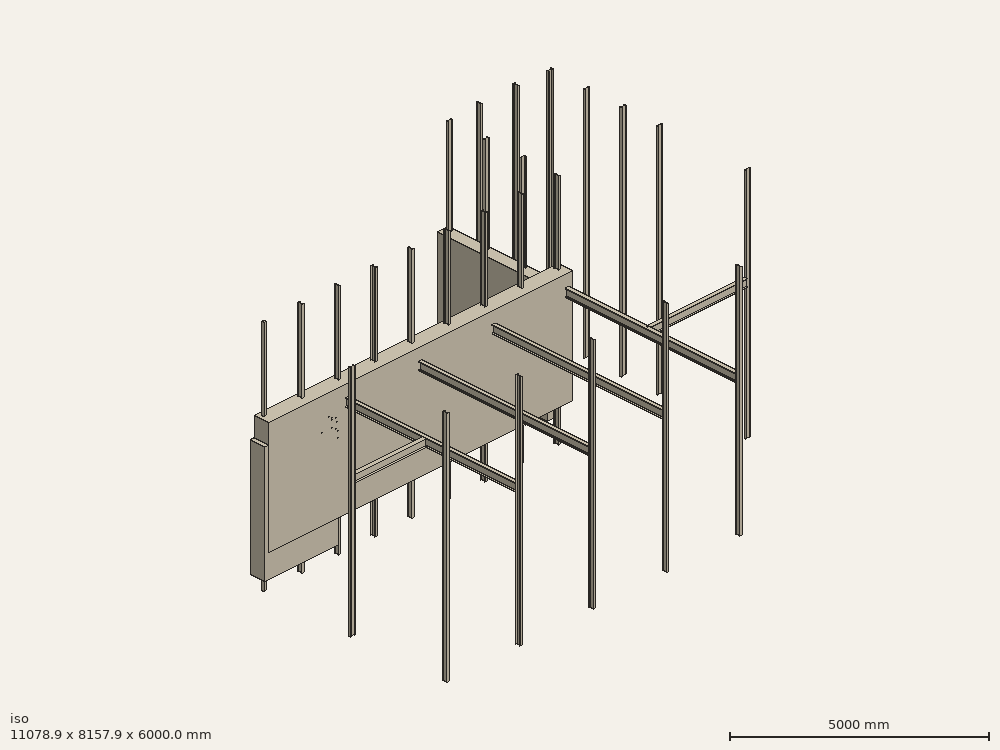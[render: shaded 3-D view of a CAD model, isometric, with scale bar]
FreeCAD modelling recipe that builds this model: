
FCSTD DOCUMENT  (FreeCAD 0.21R33321 (Git))
Label: 20230526-sunroom-layout
License: All rights reserved
LicenseURL: http://en.wikipedia.org/wiki/All_rights_reserved
objects: Part::Part2DObjectPython×75, Part::FeaturePython×34, App::DocumentObjectGroup×13, App::MeasureDistance×1, Spreadsheet::Sheet×1, App::GeometryPython×1
note: 110 computed .brp shape members not serialized (recipe doc carries the construction recipe); baked Part::Feature solids carry a one-line shape summary decoded from their .brp

FEATURE [Part::Part2DObjectPython] Rectangle001  label="Rect-sec1"  # Draft 2D object (typed FeaturePython)
  Area = 800000
  ChamferSize = 0
  Columns = 1
  FilletRadius = 0
  Height = 400
  Length = 2000
  MakeFace = true
  Placement = pos=(-5613.61,2200,0) rot=(0,0,1;0rad)
  Rows = 1
FEATURE [Part::FeaturePython] Structure001  label="fail"  # Arch/BIM 7 (typed FeaturePython)
  BaseMirror = false
  BaseOffsetX = 0
  BaseOffsetY = 0
  BasePerpendicularToTool = false
  BaseRotation = -21
  ComputedLength = 6000
  FaceMaker = 0
  Height = 64
  HorizontalArea = 4096
  IfcData = attributes={"GlobalId": {"name": "GlobalId", "type": "IfcGloballyUniqueId", "is_enum": false, "enum_values": []}, "Description": {"... (+475 chars omitted),+1 more (map truncated)
  IfcType = 7
  Length = 6000
  MoveBase = false
  MoveWithHost = false
  Nodes = (2) [(-3.54371e-32,-1.11022e-15,8.32667e-16),(6000,-1.11022e-15,8.32667e-16)]
  NodesOffset = 0
  Normal = (0,0,0)
  PerimeterLength = 256
  Placement = pos=(-5368,2460,5000) rot=(0,1,0;1.5708rad)
  PredefinedType = 0
  Profile = IPE120
  ToolOffsetFirst = 0
  ToolOffsetLast = 0
  VerticalArea = 1536000
  Width = 64
  expr: Profile = Spreadsheet.vertcoltype
FEATURE [Part::FeaturePython] Wall  label="NorthWall1-400mm"  # Arch/BIM 166 (typed FeaturePython)
  Align = 2
  Area = 0
  Base = -> Rectangle001
  BlockHeight = 0
  BlockLength = 0
  CountBroken = 0
  CountEntire = 0
  Face = 0
  Height = 3000
  HorizontalArea = 800000
  IfcData = attributes={"GlobalId": {"name": "GlobalId", "type": "IfcGloballyUniqueId", "is_enum": false, "enum_values": []}, "Description": {"... (+533 chars omitted),+1 more (map truncated)
  IfcType = 166
  Joint = 0
  Length = 0
  MakeBlocks = false
  MoveBase = false
  MoveWithHost = false
  Normal = (0,0,0)
  OffsetFirst = 0
  OffsetSecond = 0
  PerimeterLength = 4800
  Placement = pos=(0,0,-600) rot=(0,0,1;0rad)
  PredefinedType = 0
  VerticalArea = 1.44e+07
  Width = 200
FEATURE [App::MeasureDistance] Distance  label="Distance: 2363.01 mm"
  Distance = 2398.43
  P1 = (-3738.2,2140,2600)
  P2 = (-3709.77,2140,4998.26)
FEATURE [Spreadsheet::Sheet] Spreadsheet  label="S"
  cells = A1=BaseHeight; B1(BaseHeight)==5200 mm; A2=BaseLength; B2(BaseLength)==11000 mm; A3=BaseSlabThickness; B3(BaseSlabThickness)==200 mm; A4=ColHeight; B4(ColHeight)==6000 mm; A5=NorthWallThickness; B5(NorthWallThickness)==400 mm; A6=SouthWallThickness; B6(SouthWallThickness)==200 mm; A7=LaundryRoomWidth; B7(LaundryRoomWidth)==3 m; A8=LaundryRoomDepth; B8(LaundryRoomDepth)==3 m; A9=col1xpos; B9(col1xpos)==-BaseLength / 2 + 100 mm; A10=col1ypos; B10(col1ypos)==BaseHeight / 2 - NorthWallThickness / 2; A11=col1xposIPE; B11(col1xposIPE)==col1xpos + 32 mm; A12=col1yposIPE; B12(col1yposIPE)==col1ypos + 60 mm; A13=colwidth; B13(colwidth)==64 mm; A14=colheight; B14(collength)==120 mm; A15=vertcoltype; B15(vertcoltype)=IPE120
FEATURE [Part::Part2DObjectPython] Rectangle003  label="NorthWallRect"  # Draft 2D object (typed FeaturePython)
  Area = 3320000
  ChamferSize = 0
  Columns = 1
  FilletRadius = 0
  Height = 400
  Length = 8300
  MakeFace = true
  Placement = pos=(-5500,2200,0) rot=(0,0,1;0rad)
  Rows = 1
  expr: .Placement.Base.x = -Spreadsheet.BaseLength / 2
  expr: .Placement.Base.y = Spreadsheet.BaseHeight / 2 - Spreadsheet.NorthWallThickness
  expr: Height = Spreadsheet.NorthWallThickness
  expr: Length = Spreadsheet.BaseLength - 3 m + 300 mm
FEATURE [Part::Part2DObjectPython] Rectangle004  label="SouthWallRect"  # Draft 2D object (typed FeaturePython)
  Area = 2200000
  ChamferSize = 0
  Columns = 1
  FilletRadius = 0
  Height = 200
  Length = 11000
  MakeFace = true
  Placement = pos=(-5500,-2600,0) rot=(0,0,1;0rad)
  Rows = 1
  expr: .Placement.Base.x = -Spreadsheet.BaseLength / 2
  expr: .Placement.Base.y = -Spreadsheet.BaseHeight / 2
  expr: Height = Spreadsheet.SouthWallThickness
  expr: Length = Spreadsheet.BaseLength
FEATURE [Part::Part2DObjectPython] Rectangle005  label="NorthColPosRect"  # Draft 2D object (typed FeaturePython)
  Area = 960000
  ChamferSize = 0
  Columns = 1
  FilletRadius = 0
  Height = 120
  Length = 8000
  MakeFace = true
  Placement = pos=(-5500,2400,0) rot=(0,0,1;0rad)
  Rows = 1
  expr: .Placement.Base.x = -Spreadsheet.BaseLength / 2
  expr: .Placement.Base.y = Spreadsheet.BaseHeight / 2 - Spreadsheet.NorthWallThickness / 2
FEATURE [Part::Part2DObjectPython] Rectangle006  label="WestWallRect"  # Draft 2D object (typed FeaturePython)
  Area = 920000
  ChamferSize = 0
  Columns = 1
  FilletRadius = 0
  Height = 4600
  Length = 200
  MakeFace = true
  Placement = pos=(-5500,-2400,0) rot=(0,0,1;0rad)
  Rows = 1
  expr: Height = Spreadsheet.BaseHeight - Spreadsheet.NorthWallThickness - Spreadsheet.SouthWallThickness
  expr: Length = Spreadsheet.SouthWallThickness
FEATURE [Part::Part2DObjectPython] Rectangle007  label="Col1Rect"  # Draft 2D object (typed FeaturePython)
  Area = 7680
  ChamferSize = 0
  Columns = 1
  FilletRadius = 0
  Height = 120
  Length = 64
  MakeFace = true
  Placement = pos=(-5400,2400,0) rot=(0,0,1;0rad)
  Rows = 1
  expr: .Placement.Base.x = Spreadsheet.col1xpos
  expr: .Placement.Base.y = Spreadsheet.col1ypos
  expr: Height = Spreadsheet.collength
  expr: Length = Spreadsheet.colwidth
FEATURE [Part::Part2DObjectPython] Clone2D  label="Col2Rect (2D)"  # Draft 2D object (typed FeaturePython)
  Fuse = false
  Objects = -> [Rectangle007]
  Placement = pos=(-4400,2400,0) rot=(0,0,1;0rad)
  Scale = (1,1,1)
  expr: .Placement.Base.x = Spreadsheet.col1xpos + 1000 mm
  expr: .Placement.Base.y = Spreadsheet.col1ypos
FEATURE [Part::Part2DObjectPython] Clone2D001  label="Col3Rect (2D)"  # Draft 2D object (typed FeaturePython)
  Fuse = false
  Objects = -> [Rectangle007]
  Placement = pos=(-3400,2400,0) rot=(0,0,1;0rad)
  Scale = (1,1,1)
  expr: .Placement.Base.x = Spreadsheet.col1xpos + 2000 mm
FEATURE [Part::Part2DObjectPython] Clone2D002  label="Col4Rect (2D)"  # Draft 2D object (typed FeaturePython)
  Fuse = false
  Objects = -> [Rectangle007]
  Placement = pos=(-2400,2400,0) rot=(0,0,1;0rad)
  Scale = (1,1,1)
  expr: .Placement.Base.x = Spreadsheet.col1xpos + 3000 mm
  expr: .Placement.Base.y = Spreadsheet.col1ypos
FEATURE [Part::Part2DObjectPython] Clone2D003  label="Col5Rect (2D)"  # Draft 2D object (typed FeaturePython)
  Fuse = false
  Objects = -> [Rectangle007]
  Placement = pos=(-1400,2400,0) rot=(0,0,1;0rad)
  Scale = (1,1,1)
  expr: .Placement.Base.x = Spreadsheet.col1xpos + 4000 mm
  expr: .Placement.Base.y = Spreadsheet.col1ypos
FEATURE [Part::Part2DObjectPython] Clone2D004  label="Col7Rect (2D)"  # Draft 2D object (typed FeaturePython)
  Fuse = false
  Objects = -> [Rectangle007]
  Placement = pos=(600,2400,0) rot=(0,0,1;0rad)
  Scale = (1,1,1)
  expr: .Placement.Base.x = Spreadsheet.col1xpos + 6000 mm
  expr: .Placement.Base.y = Spreadsheet.col1ypos
FEATURE [Part::Part2DObjectPython] Clone2D005  label="Col6Rect (2D)"  # Draft 2D object (typed FeaturePython)
  Fuse = false
  Objects = -> [Rectangle007]
  Placement = pos=(-400,2400,0) rot=(0,0,1;0rad)
  Scale = (1,1,1)
  expr: .Placement.Base.x = Spreadsheet.col1xpos + 5000 mm
  expr: .Placement.Base.y = Spreadsheet.col1ypos
FEATURE [Part::Part2DObjectPython] Clone2D006  label="Col8Rect (2D)"  # Draft 2D object (typed FeaturePython)
  Fuse = false
  Objects = -> [Rectangle007]
  Placement = pos=(1600,2400,0) rot=(0,0,1;0rad)
  Scale = (1,1,1)
  expr: .Placement.Base.x = Spreadsheet.col1xpos + 7000 mm
  expr: .Placement.Base.y = Spreadsheet.col1ypos
FEATURE [Part::Part2DObjectPython] Rectangle008  label="LaundryRoomRect"  # Draft 2D object (typed FeaturePython)
  Area = 9000000
  ChamferSize = 0
  Columns = 1
  FilletRadius = 0
  Height = 3000
  Length = 3000
  MakeFace = true
  Placement = pos=(2500,2600,0) rot=(0,0,1;0rad)
  Rows = 1
  expr: .Placement.Base.x = 2500
  expr: Height = Spreadsheet.LaundryRoomDepth
  expr: Length = Spreadsheet.LaundryRoomDepth
FEATURE [Part::Part2DObjectPython] Clone2D007  label="Col9Rect (2D)"  # Draft 2D object (typed FeaturePython)
  Fuse = false
  Objects = -> [Rectangle007]
  Placement = pos=(2602.84,2400.21,0) rot=(0,0,1;0rad)
  Scale = (1,1,1)
FEATURE [App::DocumentObjectGroup] Group001  label="RectN"
  Group = -> [Rectangle007,Clone2D,Clone2D001,Clone2D002,Clone2D003,Clone2D005,Clone2D004,Clone2D006,Clone2D007]
FEATURE [Part::Part2DObjectPython] Clone2D008  label="Col10Rect (2D)"  # Draft 2D object (typed FeaturePython)
  Fuse = false
  Objects = -> [Clone2D007]
  Placement = pos=(2720,3400,0) rot=(0,0,1;1.5708rad)
  Scale = (1,1,1)
  expr: .Placement.Base.x = 2720 mm
  expr: .Placement.Base.y = 2400 mm + 1000 mm
FEATURE [Part::Part2DObjectPython] IPE120005  # Draft 2D object (typed FeaturePython)
  FlangeThickness = 6.3
  Height = 120
  WebThickness = 4.4
  Width = 64
FEATURE [Part::FeaturePython] Structure006  label="Col5"  # Arch/BIM 24 (typed FeaturePython)
  Base = -> IPE120005
  BaseMirror = false
  BaseOffsetX = 0
  BaseOffsetY = 0
  BasePerpendicularToTool = false
  BaseRotation = 0
  ComputedLength = 6000
  FaceMaker = 0
  Height = 6000
  HorizontalArea = 1278.96
  IfcData = attributes={"GlobalId": {"name": "GlobalId", "type": "IfcGloballyUniqueId", "is_enum": false, "enum_values": []}, "Description": {"... (+438 chars omitted),+1 more (map truncated)
  IfcType = 24
  Length = 120
  MoveBase = false
  MoveWithHost = false
  Nodes = (2) [(0,-1.61713e-15,0),(0,-1.61713e-15,6000)]
  NodesOffset = 0
  Normal = (0,0,0)
  PerimeterLength = 487.2
  Placement = pos=(-1368,2460,-1000) rot=(0,0,1;0rad)
  PredefinedType = 0
  Profile = IPE120
  ToolOffsetFirst = 0
  ToolOffsetLast = 0
  VerticalArea = 2923200
  Width = 64
  expr: .Placement.Base.x = Spreadsheet.col1xposIPE + 4000 mm
  expr: .Placement.Base.y = Spreadsheet.col1yposIPE
FEATURE [Part::Part2DObjectPython] IPE120006  # Draft 2D object (typed FeaturePython)
  FlangeThickness = 6.3
  Height = 120
  WebThickness = 4.4
  Width = 64
FEATURE [Part::FeaturePython] Structure007  label="Col6"  # Arch/BIM 24 (typed FeaturePython)
  Base = -> IPE120006
  BaseMirror = false
  BaseOffsetX = 0
  BaseOffsetY = 0
  BasePerpendicularToTool = false
  BaseRotation = 0
  ComputedLength = 6000
  FaceMaker = 0
  Height = 6000
  HorizontalArea = 1278.96
  IfcData = attributes={"GlobalId": {"name": "GlobalId", "type": "IfcGloballyUniqueId", "is_enum": false, "enum_values": []}, "Description": {"... (+438 chars omitted),+1 more (map truncated)
  IfcType = 24
  Length = 120
  MoveBase = false
  MoveWithHost = false
  Nodes = (2) [(0,-1.61713e-15,0),(0,-1.61713e-15,6000)]
  NodesOffset = 0
  Normal = (0,0,0)
  PerimeterLength = 487.2
  Placement = pos=(-368,2460,-1000) rot=(0,0,1;0rad)
  PredefinedType = 0
  Profile = IPE120
  ToolOffsetFirst = 0
  ToolOffsetLast = 0
  VerticalArea = 2923200
  Width = 64
  expr: .Placement.Base.x = Spreadsheet.col1xposIPE + 5000 mm
  expr: .Placement.Base.y = Spreadsheet.col1yposIPE
FEATURE [Part::Part2DObjectPython] IPE120007  # Draft 2D object (typed FeaturePython)
  FlangeThickness = 6.3
  Height = 120
  WebThickness = 4.4
  Width = 64
FEATURE [Part::FeaturePython] Structure008  label="Col7"  # Arch/BIM 24 (typed FeaturePython)
  Base = -> IPE120007
  BaseMirror = false
  BaseOffsetX = 0
  BaseOffsetY = 0
  BasePerpendicularToTool = false
  BaseRotation = 0
  ComputedLength = 6000
  FaceMaker = 0
  Height = 6000
  HorizontalArea = 1278.96
  IfcData = attributes={"GlobalId": {"name": "GlobalId", "type": "IfcGloballyUniqueId", "is_enum": false, "enum_values": []}, "Description": {"... (+438 chars omitted),+1 more (map truncated)
  IfcType = 24
  Length = 120
  MoveBase = false
  MoveWithHost = false
  Nodes = (2) [(0,-1.61713e-15,0),(0,-1.61713e-15,6000)]
  NodesOffset = 0
  Normal = (0,0,0)
  PerimeterLength = 487.2
  Placement = pos=(632,2460,-1000) rot=(0,0,1;0rad)
  PredefinedType = 0
  Profile = IPE120
  ToolOffsetFirst = 0
  ToolOffsetLast = 0
  VerticalArea = 2923200
  Width = 64
  expr: .Placement.Base.x = Spreadsheet.col1xposIPE + 6000 mm
  expr: .Placement.Base.y = Spreadsheet.col1yposIPE
FEATURE [Part::Part2DObjectPython] IPE120008  # Draft 2D object (typed FeaturePython)
  FlangeThickness = 6.3
  Height = 120
  WebThickness = 4.4
  Width = 64
FEATURE [Part::FeaturePython] Structure009  label="Col8"  # Arch/BIM 24 (typed FeaturePython)
  Base = -> IPE120008
  BaseMirror = false
  BaseOffsetX = 0
  BaseOffsetY = 0
  BasePerpendicularToTool = false
  BaseRotation = 0
  ComputedLength = 6000
  FaceMaker = 0
  Height = 6000
  HorizontalArea = 1278.96
  IfcData = attributes={"GlobalId": {"name": "GlobalId", "type": "IfcGloballyUniqueId", "is_enum": false, "enum_values": []}, "Description": {"... (+438 chars omitted),+1 more (map truncated)
  IfcType = 24
  Length = 120
  MoveBase = false
  MoveWithHost = false
  Nodes = (2) [(0,-1.61713e-15,0),(0,-1.61713e-15,6000)]
  NodesOffset = 0
  Normal = (0,0,0)
  PerimeterLength = 487.2
  Placement = pos=(1632,2460,-1000) rot=(0,0,1;0rad)
  PredefinedType = 0
  Profile = IPE120
  ToolOffsetFirst = 0
  ToolOffsetLast = 0
  VerticalArea = 2923200
  Width = 64
  expr: .Placement.Base.x = Spreadsheet.col1xposIPE + 7000 mm
  expr: .Placement.Base.y = Spreadsheet.col1yposIPE
FEATURE [Part::Part2DObjectPython] IPE120009  # Draft 2D object (typed FeaturePython)
  FlangeThickness = 6.3
  Height = 120
  WebThickness = 4.4
  Width = 64
FEATURE [Part::FeaturePython] Structure010  label="Col9"  # Arch/BIM 24 (typed FeaturePython)
  Base = -> IPE120009
  BaseMirror = false
  BaseOffsetX = 0
  BaseOffsetY = 0
  BasePerpendicularToTool = false
  BaseRotation = 0
  ComputedLength = 6000
  FaceMaker = 0
  Height = 6000
  HorizontalArea = 1278.96
  IfcData = attributes={"GlobalId": {"name": "GlobalId", "type": "IfcGloballyUniqueId", "is_enum": false, "enum_values": []}, "Description": {"... (+438 chars omitted),+1 more (map truncated)
  IfcType = 24
  Length = 120
  MoveBase = false
  MoveWithHost = false
  Nodes = (2) [(0,-1.61713e-15,0),(0,-1.61713e-15,6000)]
  NodesOffset = 0
  Normal = (0,0,0)
  PerimeterLength = 487.2
  Placement = pos=(2634.76,2460.15,-1000) rot=(0,0,1;0rad)
  PredefinedType = 0
  Profile = IPE120
  ToolOffsetFirst = 0
  ToolOffsetLast = 0
  VerticalArea = 2923200
  Width = 64
FEATURE [Part::Part2DObjectPython] Rectangle009  label="LaundryWallWestRect"  # Draft 2D object (typed FeaturePython)
  Area = 900000
  ChamferSize = 0
  Columns = 1
  FilletRadius = 0
  Height = 3000
  Length = 300
  MakeFace = true
  Placement = pos=(2500.39,2600,0) rot=(0,0,1;0rad)
  Rows = 1
  expr: Height = Spreadsheet.LaundryRoomDepth
FEATURE [Part::Part2DObjectPython] Clone2D009  label="Col11Rect (2D)"  # Draft 2D object (typed FeaturePython)
  Fuse = false
  Objects = -> [Clone2D008]
  Placement = pos=(2720,4400,0) rot=(0,0,1;1.5708rad)
  Scale = (1,1,1)
  expr: .Placement.Base.y = 2400 mm + 2000 mm
FEATURE [Part::Part2DObjectPython] Clone2D010  label="Col12Rect (2D)"  # Draft 2D object (typed FeaturePython)
  Fuse = false
  Objects = -> [Clone2D009]
  Placement = pos=(2720,5400,0) rot=(0,0,1;1.5708rad)
  Scale = (1,1,1)
  expr: .Placement.Base.y = 2400 mm + 3000 mm
FEATURE [Part::Part2DObjectPython] Rectangle010  label="LaundryWallEastRect"  # Draft 2D object (typed FeaturePython)
  Area = 600000
  ChamferSize = 0
  Columns = 1
  FilletRadius = 0
  Height = 3000
  Length = 200
  MakeFace = true
  Placement = pos=(5300,2600,0) rot=(0,0,1;0rad)
  Rows = 1
  expr: Height = Spreadsheet.LaundryRoomDepth
FEATURE [Part::Part2DObjectPython] Clone2D011  label="Col15Rect (2D)"  # Draft 2D object (typed FeaturePython)
  Fuse = false
  Objects = -> [Clone2D010]
  Placement = pos=(5465.32,5400,0) rot=(0,0,1;1.5708rad)
  Scale = (1,1,1)
FEATURE [Part::Part2DObjectPython] Clone2D012  label="Col16Rect (2D)"  # Draft 2D object (typed FeaturePython)
  Fuse = false
  Objects = -> [Clone2D009]
  Placement = pos=(5465.32,4400,0) rot=(0,0,1;1.5708rad)
  Scale = (1,1,1)
FEATURE [Part::Part2DObjectPython] Clone2D013  label="Col17Rect (2D)"  # Draft 2D object (typed FeaturePython)
  Fuse = false
  Objects = -> [Clone2D008]
  Placement = pos=(5465.32,3400,0) rot=(0,0,1;1.5708rad)
  Scale = (1,1,1)
FEATURE [Part::Part2DObjectPython] Clone2D014  label="Col14Rect (2D)"  # Draft 2D object (typed FeaturePython)
  Fuse = false
  Objects = -> [Clone2D006]
  Placement = pos=(4509.76,5428.53,0) rot=(0,0,1;0rad)
  Scale = (1,1,1)
FEATURE [Part::Part2DObjectPython] Clone2D015  label="Col13Rect (2D)"  # Draft 2D object (typed FeaturePython)
  Fuse = false
  Objects = -> [Clone2D004]
  Placement = pos=(3509.76,5428.53,0) rot=(0,0,1;0rad)
  Scale = (1,1,1)
FEATURE [App::DocumentObjectGroup] Group004  label="Rect"
  Group = -> [Clone2D010,Clone2D009,Clone2D008,Clone2D011,Clone2D012,Clone2D013,Clone2D014,Clone2D015]
FEATURE [Part::Part2DObjectPython] Rectangle011  label="EastWallRect"  # Draft 2D object (typed FeaturePython)
  Area = 1000000
  ChamferSize = 0
  Columns = 1
  FilletRadius = 0
  Height = 5000
  Length = 200
  MakeFace = true
  Placement = pos=(5300,-2400,0) rot=(0,0,1;0rad)
  Rows = 1
FEATURE [App::GeometryPython] BuildingPart  label="Floor"  # Arch/BIM 14 (typed FeaturePython)
  Area = 0
  CompositionType = 0
  Elevation = 0
  Group = -> [Rectangle005,Rectangle011,Rectangle004,Rectangle008,Rectangle009,Rectangle010,Rectangle006]
  Height = 0
  HeightPropagate = true
  IfcData = attributes={"GlobalId": {"name": "GlobalId", "type": "IfcGloballyUniqueId", "is_enum": false, "enum_values": []}, "Description": {"... (+866 chars omitted),+1 more (map truncated)
  IfcType = 14
  LevelOffset = 0
  LongName = Floor
  OnlySolids = true
  expr: Elevation = .Placement.Base.z
FEATURE [Part::Part2DObjectPython] Clone2D016  label="Col18Rect (2D)"  # Draft 2D object (typed FeaturePython)
  Fuse = false
  Objects = -> [Clone2D007]
  Placement = pos=(5460,2400,0) rot=(0,0,1;1.5708rad)
  Scale = (1,1,1)
FEATURE [Part::Part2DObjectPython] IPE120011  # Draft 2D object (typed FeaturePython)
  FlangeThickness = 6.3
  Height = 120
  WebThickness = 4.4
  Width = 64
FEATURE [Part::FeaturePython] Structure011  label="Col13"  # Arch/BIM 24 (typed FeaturePython)
  Base = -> IPE120011
  BaseMirror = false
  BaseOffsetX = 0
  BaseOffsetY = 0
  BasePerpendicularToTool = false
  BaseRotation = 0
  ComputedLength = 6000
  FaceMaker = 0
  Height = 6000
  HorizontalArea = 1278.96
  IfcData = attributes={"GlobalId": {"name": "GlobalId", "type": "IfcGloballyUniqueId", "is_enum": false, "enum_values": []}, "Description": {"... (+438 chars omitted),+1 more (map truncated)
  IfcType = 24
  Length = 120
  MoveBase = false
  MoveWithHost = false
  Nodes = (2) [(0,-1.61713e-15,0),(0,-1.61713e-15,6000)]
  NodesOffset = 0
  Normal = (0,0,0)
  PerimeterLength = 487.2
  Placement = pos=(3541.76,5488.53,-1000) rot=(0,0,-1;0rad)
  PredefinedType = 0
  Profile = IPE120
  ToolOffsetFirst = 0
  ToolOffsetLast = 0
  VerticalArea = 2923200
  Width = 64
FEATURE [Part::Part2DObjectPython] IPE120012  # Draft 2D object (typed FeaturePython)
  FlangeThickness = 6.3
  Height = 120
  WebThickness = 4.4
  Width = 64
FEATURE [Part::FeaturePython] Structure012  label="Col14"  # Arch/BIM 24 (typed FeaturePython)
  Base = -> IPE120012
  BaseMirror = false
  BaseOffsetX = 0
  BaseOffsetY = 0
  BasePerpendicularToTool = false
  BaseRotation = 0
  ComputedLength = 6000
  FaceMaker = 0
  Height = 6000
  HorizontalArea = 1278.96
  IfcData = attributes={"GlobalId": {"name": "GlobalId", "type": "IfcGloballyUniqueId", "is_enum": false, "enum_values": []}, "Description": {"... (+438 chars omitted),+1 more (map truncated)
  IfcType = 24
  Length = 120
  MoveBase = false
  MoveWithHost = false
  Nodes = (2) [(0,-1.61713e-15,0),(0,-1.61713e-15,6000)]
  NodesOffset = 0
  Normal = (0,0,0)
  PerimeterLength = 487.2
  Placement = pos=(4541.76,5488.53,-1000) rot=(0,0,1;0rad)
  PredefinedType = 0
  Profile = IPE120
  ToolOffsetFirst = 0
  ToolOffsetLast = 0
  VerticalArea = 2923200
  Width = 64
FEATURE [Part::Part2DObjectPython] IPE120013  # Draft 2D object (typed FeaturePython)
  FlangeThickness = 6.3
  Height = 120
  WebThickness = 4.4
  Width = 64
FEATURE [Part::FeaturePython] Structure013  label="Col12"  # Arch/BIM 24 (typed FeaturePython)
  Base = -> IPE120013
  BaseMirror = false
  BaseOffsetX = 0
  BaseOffsetY = 0
  BasePerpendicularToTool = false
  BaseRotation = 0
  ComputedLength = 6000
  FaceMaker = 0
  Height = 6000
  HorizontalArea = 1278.96
  IfcData = attributes={"GlobalId": {"name": "GlobalId", "type": "IfcGloballyUniqueId", "is_enum": false, "enum_values": []}, "Description": {"... (+438 chars omitted),+1 more (map truncated)
  IfcType = 24
  Length = 120
  MoveBase = false
  MoveWithHost = false
  Nodes = (2) [(0,-1.61713e-15,0),(0,-1.61713e-15,6000)]
  NodesOffset = 0
  Normal = (0,0,0)
  PerimeterLength = 487.2
  Placement = pos=(2660,5432,-1000) rot=(0,0,1;1.5708rad)
  PredefinedType = 0
  Profile = IPE120
  ToolOffsetFirst = 0
  ToolOffsetLast = 0
  VerticalArea = 2923200
  Width = 64
FEATURE [Part::Part2DObjectPython] IPE120014  # Draft 2D object (typed FeaturePython)
  FlangeThickness = 6.3
  Height = 120
  WebThickness = 4.4
  Width = 64
FEATURE [Part::FeaturePython] Structure014  label="Col11"  # Arch/BIM 24 (typed FeaturePython)
  Base = -> IPE120014
  BaseMirror = false
  BaseOffsetX = 0
  BaseOffsetY = 0
  BasePerpendicularToTool = false
  BaseRotation = 0
  ComputedLength = 6000
  FaceMaker = 0
  Height = 6000
  HorizontalArea = 1278.96
  IfcData = attributes={"GlobalId": {"name": "GlobalId", "type": "IfcGloballyUniqueId", "is_enum": false, "enum_values": []}, "Description": {"... (+438 chars omitted),+1 more (map truncated)
  IfcType = 24
  Length = 120
  MoveBase = false
  MoveWithHost = false
  Nodes = (2) [(0,-1.61713e-15,0),(0,-1.61713e-15,6000)]
  NodesOffset = 0
  Normal = (0,0,0)
  PerimeterLength = 487.2
  Placement = pos=(2660,4432,-1000) rot=(0,0,1;1.5708rad)
  PredefinedType = 0
  Profile = IPE120
  ToolOffsetFirst = 0
  ToolOffsetLast = 0
  VerticalArea = 2923200
  Width = 64
FEATURE [Part::Part2DObjectPython] IPE120015  # Draft 2D object (typed FeaturePython)
  FlangeThickness = 6.3
  Height = 120
  WebThickness = 4.4
  Width = 64
FEATURE [Part::FeaturePython] Structure015  label="Col10"  # Arch/BIM 24 (typed FeaturePython)
  Base = -> IPE120015
  BaseMirror = false
  BaseOffsetX = 0
  BaseOffsetY = 0
  BasePerpendicularToTool = false
  BaseRotation = 0
  ComputedLength = 6000
  FaceMaker = 0
  Height = 6000
  HorizontalArea = 1278.96
  IfcData = attributes={"GlobalId": {"name": "GlobalId", "type": "IfcGloballyUniqueId", "is_enum": false, "enum_values": []}, "Description": {"... (+438 chars omitted),+1 more (map truncated)
  IfcType = 24
  Length = 120
  MoveBase = false
  MoveWithHost = false
  Nodes = (2) [(0,-1.61713e-15,0),(0,-1.61713e-15,6000)]
  NodesOffset = 0
  Normal = (0,0,0)
  PerimeterLength = 487.2
  Placement = pos=(2660,3432,-1000) rot=(0,0,1;1.5708rad)
  PredefinedType = 0
  Profile = IPE120
  ToolOffsetFirst = 0
  ToolOffsetLast = 0
  VerticalArea = 2923200
  Width = 64
FEATURE [Part::Part2DObjectPython] IPE120016  # Draft 2D object (typed FeaturePython)
  FlangeThickness = 6.3
  Height = 120
  WebThickness = 4.4
  Width = 64
FEATURE [Part::FeaturePython] Structure016  label="Col15"  # Arch/BIM 24 (typed FeaturePython)
  Base = -> IPE120016
  BaseMirror = false
  BaseOffsetX = 0
  BaseOffsetY = 0
  BasePerpendicularToTool = false
  BaseRotation = 0
  ComputedLength = 6000
  FaceMaker = 0
  Height = 6000
  HorizontalArea = 1278.96
  IfcData = attributes={"GlobalId": {"name": "GlobalId", "type": "IfcGloballyUniqueId", "is_enum": false, "enum_values": []}, "Description": {"... (+438 chars omitted),+1 more (map truncated)
  IfcType = 24
  Length = 120
  MoveBase = false
  MoveWithHost = false
  Nodes = (2) [(0,-1.61713e-15,0),(0,-1.61713e-15,6000)]
  NodesOffset = 0
  Normal = (0,0,0)
  PerimeterLength = 487.2
  Placement = pos=(5405.32,5432,-1000) rot=(0,0,1;1.5708rad)
  PredefinedType = 0
  Profile = IPE120
  ToolOffsetFirst = 0
  ToolOffsetLast = 0
  VerticalArea = 2923200
  Width = 64
FEATURE [Part::Part2DObjectPython] IPE120017  # Draft 2D object (typed FeaturePython)
  FlangeThickness = 6.3
  Height = 120
  WebThickness = 4.4
  Width = 64
FEATURE [Part::FeaturePython] Structure017  label="Col16"  # Arch/BIM 24 (typed FeaturePython)
  Base = -> IPE120017
  BaseMirror = false
  BaseOffsetX = 0
  BaseOffsetY = 0
  BasePerpendicularToTool = false
  BaseRotation = 0
  ComputedLength = 6000
  FaceMaker = 0
  Height = 6000
  HorizontalArea = 1278.96
  IfcData = attributes={"GlobalId": {"name": "GlobalId", "type": "IfcGloballyUniqueId", "is_enum": false, "enum_values": []}, "Description": {"... (+438 chars omitted),+1 more (map truncated)
  IfcType = 24
  Length = 120
  MoveBase = false
  MoveWithHost = false
  Nodes = (2) [(0,-1.61713e-15,0),(0,-1.61713e-15,6000)]
  NodesOffset = 0
  Normal = (0,0,0)
  PerimeterLength = 487.2
  Placement = pos=(5405.27,4431.98,-1000) rot=(0,0,1;1.5708rad)
  PredefinedType = 0
  Profile = IPE120
  ToolOffsetFirst = 0
  ToolOffsetLast = 0
  VerticalArea = 2923200
  Width = 64
FEATURE [Part::Part2DObjectPython] IPE120018  # Draft 2D object (typed FeaturePython)
  FlangeThickness = 6.3
  Height = 120
  WebThickness = 4.4
  Width = 64
FEATURE [Part::FeaturePython] Structure018  label="Col17"  # Arch/BIM 24 (typed FeaturePython)
  Base = -> IPE120018
  BaseMirror = false
  BaseOffsetX = 0
  BaseOffsetY = 0
  BasePerpendicularToTool = false
  BaseRotation = 0
  ComputedLength = 6000
  FaceMaker = 0
  Height = 6000
  HorizontalArea = 1278.96
  IfcData = attributes={"GlobalId": {"name": "GlobalId", "type": "IfcGloballyUniqueId", "is_enum": false, "enum_values": []}, "Description": {"... (+438 chars omitted),+1 more (map truncated)
  IfcType = 24
  Length = 120
  MoveBase = false
  MoveWithHost = false
  Nodes = (2) [(0,-1.61713e-15,0),(0,-1.61713e-15,6000)]
  NodesOffset = 0
  Normal = (0,0,0)
  PerimeterLength = 487.2
  Placement = pos=(5405.32,3432,-1000) rot=(0,0,1;1.5708rad)
  PredefinedType = 0
  Profile = IPE120
  ToolOffsetFirst = 0
  ToolOffsetLast = 0
  VerticalArea = 2923200
  Width = 64
FEATURE [App::DocumentObjectGroup] Group006  label="ColsLaundry"
  Group = -> [Structure018,Structure011,Structure013,Structure014,Structure017,Structure016,Structure015,Structure012]
FEATURE [App::DocumentObjectGroup] Group005  label="Laundry"
  Group = -> [Group004,Group006]
FEATURE [Part::Part2DObjectPython] Rectangle012  label="LaundryWallNorth"  # Draft 2D object (typed FeaturePython)
  Area = 750000
  ChamferSize = 0
  Columns = 1
  FilletRadius = 0
  Height = 300
  Length = 2500
  MakeFace = true
  Placement = pos=(2800,5300,0) rot=(0,0,1;0rad)
  Rows = 1
FEATURE [Part::Part2DObjectPython] Rectangle013  label="LaundryFloorSlabRect"  # Draft 2D object (typed FeaturePython)
  Area = 6750000
  ChamferSize = 0
  Columns = 1
  FilletRadius = 0
  Height = 2700
  Length = 2500
  MakeFace = true
  Placement = pos=(2802.36,2601.58,0) rot=(0,0,1;0rad)
  Rows = 1
FEATURE [Part::Part2DObjectPython] IPE120019  # Draft 2D object (typed FeaturePython)
  FlangeThickness = 6.3
  Height = 120
  WebThickness = 4.4
  Width = 64
FEATURE [Part::FeaturePython] Structure019  label="Col18"  # Arch/BIM 24 (typed FeaturePython)
  Base = -> IPE120019
  BaseMirror = false
  BaseOffsetX = 0
  BaseOffsetY = 0
  BasePerpendicularToTool = false
  BaseRotation = 0
  ComputedLength = 6000
  FaceMaker = 0
  Height = 6000
  HorizontalArea = 1278.96
  IfcData = attributes={"GlobalId": {"name": "GlobalId", "type": "IfcGloballyUniqueId", "is_enum": false, "enum_values": []}, "Description": {"... (+438 chars omitted),+1 more (map truncated)
  IfcType = 24
  Length = 120
  MoveBase = false
  MoveWithHost = false
  Nodes = (2) [(0,-1.61713e-15,0),(0,-1.61713e-15,6000)]
  NodesOffset = 0
  Normal = (0,0,0)
  PerimeterLength = 487.2
  Placement = pos=(5400,2432,-1000) rot=(0,0,1;1.5708rad)
  PredefinedType = 0
  Profile = IPE120
  ToolOffsetFirst = 0
  ToolOffsetLast = 0
  VerticalArea = 2923200
  Width = 64
FEATURE [Part::Part2DObjectPython] Clone2D017  label="Col31Rect"  # Draft 2D object (typed FeaturePython)
  Fuse = false
  Objects = -> [Rectangle007]
  Placement = pos=(-5400,-2557.73,0) rot=(0,0,1;0rad)
  Scale = (1,1,1)
  expr: .Placement.Base.x = Spreadsheet.col1xpos
FEATURE [Part::Part2DObjectPython] Clone2D018  label="Col30Rect"  # Draft 2D object (typed FeaturePython)
  Fuse = false
  Objects = -> [Clone2D]
  Placement = pos=(-4400,-2557.73,0) rot=(0,0,1;0rad)
  Scale = (1,1,1)
  expr: .Placement.Base.x = Spreadsheet.col1xpos + 1000 mm
FEATURE [Part::Part2DObjectPython] Clone2D019  label="Col29Rect"  # Draft 2D object (typed FeaturePython)
  Fuse = false
  Objects = -> [Clone2D001]
  Placement = pos=(-3400,-2557.73,0) rot=(0,0,1;0rad)
  Scale = (1,1,1)
  expr: .Placement.Base.x = Spreadsheet.col1xpos + 2000 mm
FEATURE [Part::Part2DObjectPython] Clone2D020  label="Col28Rect"  # Draft 2D object (typed FeaturePython)
  Fuse = false
  Objects = -> [Clone2D002]
  Placement = pos=(-2400,-2557.73,0) rot=(0,0,1;0rad)
  Scale = (1,1,1)
  expr: .Placement.Base.x = Spreadsheet.col1xpos + 3000 mm
FEATURE [Part::Part2DObjectPython] Clone2D021  label="Col27Rect"  # Draft 2D object (typed FeaturePython)
  Fuse = false
  Objects = -> [Clone2D003]
  Placement = pos=(-1400,-2557.73,0) rot=(0,0,1;0rad)
  Scale = (1,1,1)
  expr: .Placement.Base.x = Spreadsheet.col1xpos + 4000 mm
FEATURE [Part::Part2DObjectPython] Clone2D022  label="Col26Rect"  # Draft 2D object (typed FeaturePython)
  Fuse = false
  Objects = -> [Clone2D005]
  Placement = pos=(-400,-2557.73,0) rot=(0,0,1;0rad)
  Scale = (1,1,1)
  expr: .Placement.Base.x = Spreadsheet.col1xpos + 5000 mm
FEATURE [Part::Part2DObjectPython] Clone2D023  label="Col25Rect"  # Draft 2D object (typed FeaturePython)
  Fuse = false
  Objects = -> [Clone2D004]
  Placement = pos=(570.338,-2557.73,0) rot=(0,0,1;0rad)
  Scale = (1,1,1)
FEATURE [Part::Part2DObjectPython] Clone2D025  label="Col24Rect"  # Draft 2D object (typed FeaturePython)
  Fuse = false
  Objects = -> [Clone2D020]
  Placement = pos=(1599.92,-2557.73,0) rot=(0,0,1;0rad)
  Scale = (1,1,1)
FEATURE [Part::Part2DObjectPython] Clone2D026  label="Col23Rect"  # Draft 2D object (typed FeaturePython)
  Fuse = false
  Objects = -> [Clone2D021]
  Placement = pos=(2599.92,-2557.73,0) rot=(0,0,1;0rad)
  Scale = (1,1,1)
FEATURE [Part::Part2DObjectPython] Clone2D027  label="Col22Rect"  # Draft 2D object (typed FeaturePython)
  Fuse = false
  Objects = -> [Clone2D022]
  Placement = pos=(3599.92,-2557.73,0) rot=(0,0,1;0rad)
  Scale = (1,1,1)
FEATURE [Part::Part2DObjectPython] Clone2D028  label="Col21Rect"  # Draft 2D object (typed FeaturePython)
  Fuse = false
  Objects = -> [Clone2D023]
  Placement = pos=(4570.26,-2557.73,0) rot=(0,0,1;0rad)
  Scale = (1,1,1)
FEATURE [Part::Part2DObjectPython] Clone2D029  label="Col20Rect"  # Draft 2D object (typed FeaturePython)
  Fuse = false
  Placement = pos=(5460.05,-2532.3,0) rot=(0,0,1;1.5708rad)
  Scale = (1,1,1)
FEATURE [Part::Part2DObjectPython] Clone2D030  label="Col19Rect"  # Draft 2D object (typed FeaturePython)
  Fuse = false
  Objects = -> [Clone2D016]
  Placement = pos=(5460,0,0) rot=(0,0,1;1.5708rad)
  Scale = (1,1,1)
FEATURE [Part::Part2DObjectPython] Clone2D031  label="Col32Rect"  # Draft 2D object (typed FeaturePython)
  Fuse = false
  Objects = -> [Clone2D030]
  Placement = pos=(-5340,0,0) rot=(0,0,1;1.5708rad)
  Scale = (1,1,1)
FEATURE [App::DocumentObjectGroup] Group008  label="RectS"
  Group = -> [Clone2D017,Clone2D018,Clone2D019,Clone2D020,Clone2D021,Clone2D022,Clone2D023,Clone2D025,Clone2D026,Clone2D027,Clone2D028,Clone2D031]
FEATURE [App::DocumentObjectGroup] Group002  label="South"
  Group = -> [Group008]
FEATURE [Part::Part2DObjectPython] IPE120020  # Draft 2D object (typed FeaturePython)
  FlangeThickness = 6.3
  Height = 120
  WebThickness = 4.4
  Width = 64
FEATURE [Part::FeaturePython] Structure020  label="Col29"  # Arch/BIM 24 (typed FeaturePython)
  Base = -> IPE120020
  BaseMirror = false
  BaseOffsetX = 0
  BaseOffsetY = 0
  BasePerpendicularToTool = false
  BaseRotation = 0
  ComputedLength = 6000
  FaceMaker = 0
  Height = 6000
  HorizontalArea = 1278.96
  IfcData = attributes={"GlobalId": {"name": "GlobalId", "type": "IfcGloballyUniqueId", "is_enum": false, "enum_values": []}, "Description": {"... (+438 chars omitted),+1 more (map truncated)
  IfcType = 24
  Length = 120
  MoveBase = false
  MoveWithHost = false
  Nodes = (2) [(0,-1.61713e-15,0),(0,-1.61713e-15,6000)]
  NodesOffset = 0
  Normal = (0,0,0)
  PerimeterLength = 487.2
  Placement = pos=(-3368,-2497.73,-1000) rot=(0,0,1;0rad)
  PredefinedType = 0
  Profile = IPE120
  ToolOffsetFirst = 0
  ToolOffsetLast = 0
  VerticalArea = 2923200
  Width = 64
FEATURE [Part::Part2DObjectPython] IPE120021  # Draft 2D object (typed FeaturePython)
  FlangeThickness = 6.3
  Height = 120
  WebThickness = 4.4
  Width = 64
FEATURE [Part::FeaturePython] Structure021  label="Col27"  # Arch/BIM 24 (typed FeaturePython)
  Base = -> IPE120021
  BaseMirror = false
  BaseOffsetX = 0
  BaseOffsetY = 0
  BasePerpendicularToTool = false
  BaseRotation = 0
  ComputedLength = 6000
  FaceMaker = 0
  Height = 6000
  HorizontalArea = 1278.96
  IfcData = attributes={"GlobalId": {"name": "GlobalId", "type": "IfcGloballyUniqueId", "is_enum": false, "enum_values": []}, "Description": {"... (+438 chars omitted),+1 more (map truncated)
  IfcType = 24
  Length = 120
  MoveBase = false
  MoveWithHost = false
  Nodes = (2) [(0,-1.61713e-15,0),(0,-1.61713e-15,6000)]
  NodesOffset = 0
  Normal = (0,0,0)
  PerimeterLength = 487.2
  Placement = pos=(-1368,-2497.65,-1000) rot=(0,0,1;0rad)
  PredefinedType = 0
  Profile = IPE120
  ToolOffsetFirst = 0
  ToolOffsetLast = 0
  VerticalArea = 2923200
  Width = 64
FEATURE [Part::Part2DObjectPython] IPE120022  # Draft 2D object (typed FeaturePython)
  FlangeThickness = 6.3
  Height = 120
  WebThickness = 4.4
  Width = 64
FEATURE [Part::FeaturePython] Structure022  label="Col25"  # Arch/BIM 24 (typed FeaturePython)
  Base = -> IPE120022
  BaseMirror = false
  BaseOffsetX = 0
  BaseOffsetY = 0
  BasePerpendicularToTool = false
  BaseRotation = 0
  ComputedLength = 6000
  FaceMaker = 0
  Height = 6000
  HorizontalArea = 1278.96
  IfcData = attributes={"GlobalId": {"name": "GlobalId", "type": "IfcGloballyUniqueId", "is_enum": false, "enum_values": []}, "Description": {"... (+438 chars omitted),+1 more (map truncated)
  IfcType = 24
  Length = 120
  MoveBase = false
  MoveWithHost = false
  Nodes = (2) [(0,-1.61713e-15,0),(0,-1.61713e-15,6000)]
  NodesOffset = 0
  Normal = (0,0,0)
  PerimeterLength = 487.2
  Placement = pos=(630.27,-2497.92,-1000) rot=(0,0,1;0rad)
  PredefinedType = 0
  Profile = IPE120
  ToolOffsetFirst = 0
  ToolOffsetLast = 0
  VerticalArea = 2923200
  Width = 64
FEATURE [Part::Part2DObjectPython] IPE120023  # Draft 2D object (typed FeaturePython)
  FlangeThickness = 6.3
  Height = 120
  WebThickness = 4.4
  Width = 64
FEATURE [Part::FeaturePython] Structure023  label="Col23"  # Arch/BIM 24 (typed FeaturePython)
  Base = -> IPE120023
  BaseMirror = false
  BaseOffsetX = 0
  BaseOffsetY = 0
  BasePerpendicularToTool = false
  BaseRotation = 0
  ComputedLength = 6000
  FaceMaker = 0
  Height = 6000
  HorizontalArea = 1278.96
  IfcData = attributes={"GlobalId": {"name": "GlobalId", "type": "IfcGloballyUniqueId", "is_enum": false, "enum_values": []}, "Description": {"... (+438 chars omitted),+1 more (map truncated)
  IfcType = 24
  Length = 120
  MoveBase = false
  MoveWithHost = false
  Nodes = (2) [(0,-1.61713e-15,0),(0,-1.61713e-15,6000)]
  NodesOffset = 0
  Normal = (0,0,0)
  PerimeterLength = 487.2
  Placement = pos=(2631.92,-2497.73,-1000) rot=(0,0,1;0rad)
  PredefinedType = 0
  Profile = IPE120
  ToolOffsetFirst = 0
  ToolOffsetLast = 0
  VerticalArea = 2923200
  Width = 64
FEATURE [Part::Part2DObjectPython] IPE120024  # Draft 2D object (typed FeaturePython)
  FlangeThickness = 6.3
  Height = 120
  WebThickness = 4.4
  Width = 64
FEATURE [Part::FeaturePython] Structure024  label="Col19"  # Arch/BIM 24 (typed FeaturePython)
  Base = -> IPE120024
  BaseMirror = false
  BaseOffsetX = 0
  BaseOffsetY = 0
  BasePerpendicularToTool = false
  BaseRotation = 0
  ComputedLength = 6000
  FaceMaker = 0
  Height = 6000
  HorizontalArea = 1278.96
  IfcData = attributes={"GlobalId": {"name": "GlobalId", "type": "IfcGloballyUniqueId", "is_enum": false, "enum_values": []}, "Description": {"... (+438 chars omitted),+1 more (map truncated)
  IfcType = 24
  Length = 120
  MoveBase = false
  MoveWithHost = false
  Nodes = (2) [(0,-1.61713e-15,0),(0,-1.61713e-15,6000)]
  NodesOffset = 0
  Normal = (0,0,0)
  PerimeterLength = 487.2
  Placement = pos=(5400,32,-1000) rot=(0,0,1;1.5708rad)
  PredefinedType = 0
  Profile = IPE120
  ToolOffsetFirst = 0
  ToolOffsetLast = 0
  VerticalArea = 2923200
  Width = 64
FEATURE [App::DocumentObjectGroup] Group010  label="ColE"
  Group = -> [Structure024]
FEATURE [App::DocumentObjectGroup] Group011  label="RectE"
  Group = -> [Clone2D029,Clone2D030]
FEATURE [App::DocumentObjectGroup] Group009  label="East"
  Group = -> [Group010,Group011]
FEATURE [Part::Part2DObjectPython] IPE120025  # Draft 2D object (typed FeaturePython)
  FlangeThickness = 6.3
  Height = 120
  WebThickness = 4.4
  Width = 64
FEATURE [Part::FeaturePython] Structure025  label="Col31"  # Arch/BIM 24 (typed FeaturePython)
  Base = -> IPE120025
  BaseMirror = false
  BaseOffsetX = 0
  BaseOffsetY = 0
  BasePerpendicularToTool = false
  BaseRotation = 0
  ComputedLength = 6000
  FaceMaker = 0
  Height = 6000
  HorizontalArea = 1278.96
  IfcData = attributes={"GlobalId": {"name": "GlobalId", "type": "IfcGloballyUniqueId", "is_enum": false, "enum_values": []}, "Description": {"... (+438 chars omitted),+1 more (map truncated)
  IfcType = 24
  Length = 120
  MoveBase = false
  MoveWithHost = false
  Nodes = (2) [(0,-1.61713e-15,0),(0,-1.61713e-15,6000)]
  NodesOffset = 0
  Normal = (0,0,0)
  PerimeterLength = 487.2
  Placement = pos=(-5368,-2497.73,-1000) rot=(0,0,1;0rad)
  PredefinedType = 0
  Profile = IPE120
  ToolOffsetFirst = 0
  ToolOffsetLast = 0
  VerticalArea = 2923200
  Width = 64
FEATURE [Part::Part2DObjectPython] IPE120026  # Draft 2D object (typed FeaturePython)
  FlangeThickness = 6.3
  Height = 120
  WebThickness = 4.4
  Width = 64
FEATURE [Part::FeaturePython] Structure026  label="Col32"  # Arch/BIM 24 (typed FeaturePython)
  Base = -> IPE120026
  BaseMirror = false
  BaseOffsetX = 0
  BaseOffsetY = 0
  BasePerpendicularToTool = false
  BaseRotation = 0
  ComputedLength = 6000
  FaceMaker = 0
  Height = 6000
  HorizontalArea = 1278.96
  IfcData = attributes={"GlobalId": {"name": "GlobalId", "type": "IfcGloballyUniqueId", "is_enum": false, "enum_values": []}, "Description": {"... (+438 chars omitted),+1 more (map truncated)
  IfcType = 24
  Length = 120
  MoveBase = false
  MoveWithHost = false
  Nodes = (2) [(0,-1.61713e-15,0),(0,-1.61713e-15,6000)]
  NodesOffset = 0
  Normal = (0,0,0)
  PerimeterLength = 487.2
  Placement = pos=(-5400,32,-1000) rot=(0,0,1;1.5708rad)
  PredefinedType = 0
  Profile = IPE120
  ToolOffsetFirst = 0
  ToolOffsetLast = 0
  VerticalArea = 2923200
  Width = 64
FEATURE [Part::Part2DObjectPython] IPE120028  # Draft 2D object (typed FeaturePython)
  FlangeThickness = 8.5
  Height = 200
  WebThickness = 5.6
  Width = 100
FEATURE [Part::FeaturePython] Structure028  label="Beam2-IPE200"  # Arch/BIM 7 (typed FeaturePython)
  Base = -> IPE120028
  BaseMirror = false
  BaseOffsetX = 0
  BaseOffsetY = 0
  BasePerpendicularToTool = false
  BaseRotation = 0
  ComputedLength = 4838
  FaceMaker = 0
  Height = 4838
  HorizontalArea = 940507
  IfcData = attributes={"GlobalId": {"name": "GlobalId", "type": "IfcGloballyUniqueId", "is_enum": false, "enum_values": []}, "Description": {"... (+475 chars omitted),+1 more (map truncated)
  IfcType = 7
  Length = 200
  MoveBase = false
  MoveWithHost = false
  Nodes = (2) [(0,-1.95917e-14,0),(0,-1.95917e-14,4838)]
  NodesOffset = 0
  Normal = (0,0,0)
  PerimeterLength = 0
  Placement = pos=(-1368.82,2400.24,2500) rot=(1,0,0;1.5708rad)
  PredefinedType = 0
  Profile = IPE200
  ToolOffsetFirst = 0
  ToolOffsetLast = 0
  VerticalArea = 1.94065e+06
  Width = 100
FEATURE [Part::Part2DObjectPython] IPE120029  # Draft 2D object (typed FeaturePython)
  FlangeThickness = 8.5
  Height = 200
  WebThickness = 5.6
  Width = 100
FEATURE [Part::FeaturePython] Structure029  label="Beam4-IPE200"  # Arch/BIM 7 (typed FeaturePython)
  Base = -> IPE120029
  BaseMirror = false
  BaseOffsetX = 0
  BaseOffsetY = 0
  BasePerpendicularToTool = false
  BaseRotation = 0
  ComputedLength = 4838
  FaceMaker = 0
  Height = 4838
  HorizontalArea = 940507
  IfcData = attributes={"GlobalId": {"name": "GlobalId", "type": "IfcGloballyUniqueId", "is_enum": false, "enum_values": []}, "Description": {"... (+475 chars omitted),+1 more (map truncated)
  IfcType = 7
  Length = 200
  MoveBase = false
  MoveWithHost = false
  Nodes = (2) [(0,-1.95917e-14,0),(0,-1.95917e-14,4838)]
  NodesOffset = 0
  Normal = (0,0,0)
  PerimeterLength = 0
  Placement = pos=(2634.93,2400.2,2500) rot=(1,0,0;1.5708rad)
  PredefinedType = 0
  Profile = IPE200
  ToolOffsetFirst = 0
  ToolOffsetLast = 0
  VerticalArea = 1.94065e+06
  Width = 100
FEATURE [Part::FeaturePython] Wall002  label="NorthWall"  # Arch/BIM 166 (typed FeaturePython)
  Align = 2
  Area = 0
  Base = -> Rectangle003
  BlockHeight = 0
  BlockLength = 0
  CountBroken = 0
  CountEntire = 0
  Face = 0
  Height = 2900
  HorizontalArea = 3320000
  IfcData = attributes={"GlobalId": {"name": "GlobalId", "type": "IfcGloballyUniqueId", "is_enum": false, "enum_values": []}, "Description": {"... (+533 chars omitted),+1 more (map truncated)
  IfcType = 166
  Joint = 0
  Length = 0
  MakeBlocks = false
  MoveBase = false
  MoveWithHost = false
  Normal = (0,0,0)
  OffsetFirst = 0
  OffsetSecond = 0
  PerimeterLength = 17400
  PredefinedType = 0
  VerticalArea = 50460000
  Width = 200
FEATURE [Part::FeaturePython] Wall003  label="Wall"  # Arch/BIM 166 (typed FeaturePython)
  Align = 2
  Area = 0
  Base = -> Rectangle009
  BlockHeight = 0
  BlockLength = 0
  CountBroken = 0
  CountEntire = 0
  Face = 0
  Height = 3000
  HorizontalArea = 900000
  IfcData = attributes={"GlobalId": {"name": "GlobalId", "type": "IfcGloballyUniqueId", "is_enum": false, "enum_values": []}, "Description": {"... (+533 chars omitted),+1 more (map truncated)
  IfcType = 166
  Joint = 0
  Length = 0
  MakeBlocks = false
  MoveBase = false
  MoveWithHost = false
  Normal = (0,0,0)
  OffsetFirst = 0
  OffsetSecond = 0
  PerimeterLength = 6600
  Placement = pos=(0,0,-500) rot=(0,0,1;0rad)
  PredefinedType = 0
  VerticalArea = 19800000
  Width = 200
FEATURE [Part::Part2DObjectPython] IPE200001  # Draft 2D object (typed FeaturePython)
  FlangeThickness = 8.5
  Height = 200
  WebThickness = 5.6
  Width = 100
FEATURE [Part::FeaturePython] Structure  label="Beam5"  # Arch/BIM 24 (typed FeaturePython)
  Base = -> IPE200001
  BaseMirror = false
  BaseOffsetX = 0
  BaseOffsetY = 0
  BasePerpendicularToTool = false
  BaseRotation = 0
  ComputedLength = 1930
  FaceMaker = 0
  Height = 1930
  HorizontalArea = 375192
  IfcData = attributes={"GlobalId": {"name": "GlobalId", "type": "IfcGloballyUniqueId", "is_enum": false, "enum_values": []}, "Description": {"... (+438 chars omitted),+1 more (map truncated)
  IfcType = 24
  Length = 200
  MoveBase = false
  MoveWithHost = false
  Nodes = (2) [(0,-1.95917e-14,0),(0,-1.95917e-14,1930)]
  NodesOffset = 0
  Normal = (0,0,0)
  PerimeterLength = 0
  Placement = pos=(-5340,29.43,2500) rot=(0.57735,0.57735,0.57735;2.0944rad)
  PredefinedType = 0
  Profile = IPE200
  ToolOffsetFirst = 0
  ToolOffsetLast = 0
  VerticalArea = 777450
  Width = 100
FEATURE [Part::Part2DObjectPython] IPE200002  # Draft 2D object (typed FeaturePython)
  FlangeThickness = 8.5
  Height = 200
  WebThickness = 5.6
  Width = 100
FEATURE [Part::FeaturePython] Structure030  label="Beam6"  # Arch/BIM 24 (typed FeaturePython)
  Base = -> IPE200002
  BaseMirror = false
  BaseOffsetX = 0
  BaseOffsetY = 0
  BasePerpendicularToTool = false
  BaseRotation = 0
  ComputedLength = 2700
  FaceMaker = 0
  Height = 2700
  HorizontalArea = 524880
  IfcData = attributes={"GlobalId": {"name": "GlobalId", "type": "IfcGloballyUniqueId", "is_enum": false, "enum_values": []}, "Description": {"... (+438 chars omitted),+1 more (map truncated)
  IfcType = 24
  Length = 200
  MoveBase = false
  MoveWithHost = false
  Nodes = (2) [(0,-1.95917e-14,0),(0,-1.95917e-14,2700)]
  NodesOffset = 0
  Normal = (0,0,0)
  PerimeterLength = 0
  Placement = pos=(5340,10.71,2500) rot=(0.57735,-0.57735,-0.57735;2.0944rad)
  PredefinedType = 0
  Profile = IPE200
  ToolOffsetFirst = 0
  ToolOffsetLast = 0
  VerticalArea = 1.08545e+06
  Width = 100
FEATURE [Part::Part2DObjectPython] Rectangle  label="Base"  # Draft 2D object (typed FeaturePython)
  Area = 57200000
  ChamferSize = 0
  Columns = 1
  FilletRadius = 0
  Height = 5200
  Length = 11000
  MakeFace = true
  Placement = pos=(-5500,-2600,0) rot=(0,0,1;0rad)
  Rows = 1
  expr: .Placement.Base.x = -Spreadsheet.BaseLength / 2
  expr: .Placement.Base.y = -Spreadsheet.BaseHeight / 2
  expr: Height = Spreadsheet.BaseHeight
  expr: Length = Spreadsheet.BaseLength
FEATURE [Part::Part2DObjectPython] IPE120004  # Draft 2D object (typed FeaturePython)
  FlangeThickness = 6.3
  Height = 120
  WebThickness = 4.4
  Width = 64
FEATURE [Part::FeaturePython] Structure005  label="Col4"  # Arch/BIM 7 (typed FeaturePython)
  Base = -> IPE120004
  BaseMirror = false
  BaseOffsetX = 0
  BaseOffsetY = 0
  BasePerpendicularToTool = false
  BaseRotation = 0
  ComputedLength = 6000
  FaceMaker = 0
  Height = 6000
  HorizontalArea = 1278.96
  IfcData = attributes={"GlobalId": {"name": "GlobalId", "type": "IfcGloballyUniqueId", "is_enum": false, "enum_values": []}, "Description": {"... (+475 chars omitted),+1 more (map truncated)
  IfcType = 7
  Length = 120
  MoveBase = false
  MoveWithHost = false
  Nodes = (2) [(0,-1.61713e-15,0),(0,-1.61713e-15,6000)]
  NodesOffset = 0
  Normal = (0,0,0)
  PerimeterLength = 487.2
  Placement = pos=(-2368,2460,-1000) rot=(0,0,1;0rad)
  PredefinedType = 0
  Profile = IPE120
  ToolOffsetFirst = 0
  ToolOffsetLast = 0
  VerticalArea = 2923200
  Width = 64
  expr: .Placement.Base.x = Spreadsheet.col1xposIPE + 3000 mm
  expr: .Placement.Base.y = Spreadsheet.col1yposIPE
  expr: Height = Spreadsheet.ColHeight
FEATURE [Part::Part2DObjectPython] IPE120027  label="IPE2003"  # Draft 2D object (typed FeaturePython)
  FlangeThickness = 8.5
  Height = 200
  WebThickness = 5.6
  Width = 100
FEATURE [Part::FeaturePython] Structure027  label="Beam3-IPE200"  # Arch/BIM 7 (typed FeaturePython)
  Base = -> IPE120027
  BaseMirror = false
  BaseOffsetX = 0
  BaseOffsetY = 0
  BasePerpendicularToTool = false
  BaseRotation = 0
  ComputedLength = 4838
  FaceMaker = 0
  Height = 4838
  HorizontalArea = 940507
  IfcData = attributes={"GlobalId": {"name": "GlobalId", "type": "IfcGloballyUniqueId", "is_enum": false, "enum_values": []}, "Description": {"... (+475 chars omitted),+1 more (map truncated)
  IfcType = 7
  Length = 200
  MoveBase = false
  MoveWithHost = false
  Nodes = (2) [(0,-1.95917e-14,0),(0,-1.95917e-14,4838)]
  NodesOffset = 0
  Normal = (0,0,0)
  PerimeterLength = 0
  Placement = pos=(633.192,2400.06,2500) rot=(1,0,0;1.5708rad)
  PredefinedType = 0
  Profile = IPE200
  ToolOffsetFirst = 0
  ToolOffsetLast = 0
  VerticalArea = 1.94065e+06
  Width = 100
FEATURE [Part::Part2DObjectPython] IPE120003  # Draft 2D object (typed FeaturePython)
  FlangeThickness = 6.3
  Height = 120
  WebThickness = 4.4
  Width = 64
FEATURE [Part::FeaturePython] Structure004  label="Col3"  # Arch/BIM 7 (typed FeaturePython)
  Base = -> IPE120003
  BaseMirror = false
  BaseOffsetX = 0
  BaseOffsetY = 0
  BasePerpendicularToTool = false
  BaseRotation = 0
  ComputedLength = 6000
  FaceMaker = 0
  Height = 6000
  HorizontalArea = 1278.96
  IfcData = attributes={"GlobalId": {"name": "GlobalId", "type": "IfcGloballyUniqueId", "is_enum": false, "enum_values": []}, "Description": {"... (+475 chars omitted),+1 more (map truncated)
  IfcType = 7
  Length = 120
  MoveBase = false
  MoveWithHost = false
  Nodes = (2) [(0,-1.61713e-15,0),(0,-1.61713e-15,6000)]
  NodesOffset = 0
  Normal = (0,0,0)
  PerimeterLength = 487.2
  Placement = pos=(-3368,2460,-1000) rot=(0,0,1;0rad)
  PredefinedType = 0
  Profile = IPE120
  ToolOffsetFirst = 0
  ToolOffsetLast = 0
  VerticalArea = 2923200
  Width = 64
  expr: .Placement.Base.x = Spreadsheet.col1xposIPE + 2000 mm
  expr: .Placement.Base.y = Spreadsheet.col1yposIPE
  expr: Height = Spreadsheet.ColHeight
FEATURE [Part::Part2DObjectPython] IPE120002  # Draft 2D object (typed FeaturePython)
  FlangeThickness = 6.3
  Height = 120
  WebThickness = 4.4
  Width = 64
FEATURE [Part::FeaturePython] Structure003  label="Col2"  # Arch/BIM 7 (typed FeaturePython)
  Base = -> IPE120002
  BaseMirror = false
  BaseOffsetX = 0
  BaseOffsetY = 0
  BasePerpendicularToTool = false
  BaseRotation = 0
  ComputedLength = 6000
  FaceMaker = 0
  Height = 6000
  HorizontalArea = 1278.96
  IfcData = attributes={"GlobalId": {"name": "GlobalId", "type": "IfcGloballyUniqueId", "is_enum": false, "enum_values": []}, "Description": {"... (+475 chars omitted),+1 more (map truncated)
  IfcType = 7
  Length = 120
  MoveBase = false
  MoveWithHost = false
  Nodes = (2) [(0,-1.61713e-15,0),(0,-1.61713e-15,6000)]
  NodesOffset = 0
  Normal = (0,0,0)
  PerimeterLength = 487.2
  Placement = pos=(-4368,2460,-1000) rot=(0,0,1;0rad)
  PredefinedType = 0
  Profile = IPE120
  ToolOffsetFirst = 0
  ToolOffsetLast = 0
  VerticalArea = 2923200
  Width = 64
  expr: .Placement.Base.x = Spreadsheet.col1xposIPE + 1000 mm
  expr: .Placement.Base.y = Spreadsheet.col1yposIPE
  expr: Height = Spreadsheet.ColHeight
FEATURE [App::DocumentObjectGroup] Group003  label="ColsN"
  Group = -> [Structure001,Structure003,Structure004,Structure005,Structure006,Structure007,Structure008,Structure009,Structure010]
FEATURE [App::DocumentObjectGroup] Group007  label="North"
  Group = -> [Group001,Group003]
FEATURE [App::DocumentObjectGroup] Group  label="Columns"
  Group = -> [Group002,Group005,Group007,Group009]
FEATURE [Part::Part2DObjectPython] IPE200  # Draft 2D object (typed FeaturePython)
  FlangeThickness = 8.5
  Height = 200
  WebThickness = 5.6
  Width = 100
FEATURE [Part::FeaturePython] Structure002  label="Beam1-IPE200"  # Arch/BIM 7 (typed FeaturePython)
  Base = -> IPE200
  BaseMirror = false
  BaseOffsetX = 0
  BaseOffsetY = 0
  BasePerpendicularToTool = false
  BaseRotation = 0
  ComputedLength = 4838
  FaceMaker = 0
  Height = 4838
  HorizontalArea = 940507
  IfcData = attributes={"GlobalId": {"name": "GlobalId", "type": "IfcGloballyUniqueId", "is_enum": false, "enum_values": []}, "Description": {"... (+475 chars omitted),+1 more (map truncated)
  IfcType = 7
  Length = 200
  MoveBase = false
  MoveWithHost = false
  Nodes = (2) [(0,-1.95917e-14,0),(0,-1.95917e-14,4838)]
  NodesOffset = 0
  Normal = (0,0,0)
  PerimeterLength = 0
  Placement = pos=(-3367.32,2400,2500) rot=(1,0,0;1.5708rad)
  PredefinedType = 0
  Profile = IPE200
  ToolOffsetFirst = 0
  ToolOffsetLast = 0
  VerticalArea = 1.94065e+06
  Width = 100
FEATURE [App::DocumentObjectGroup] Group012  label="Beams"
  Group = -> [Structure027,Structure028,Structure029,Structure002]
FEATURE [Part::Part2DObjectPython] IPE200003  # Draft 2D object (typed FeaturePython)
  FlangeThickness = 8.5
  Height = 200
  WebThickness = 5.6
  Width = 100
